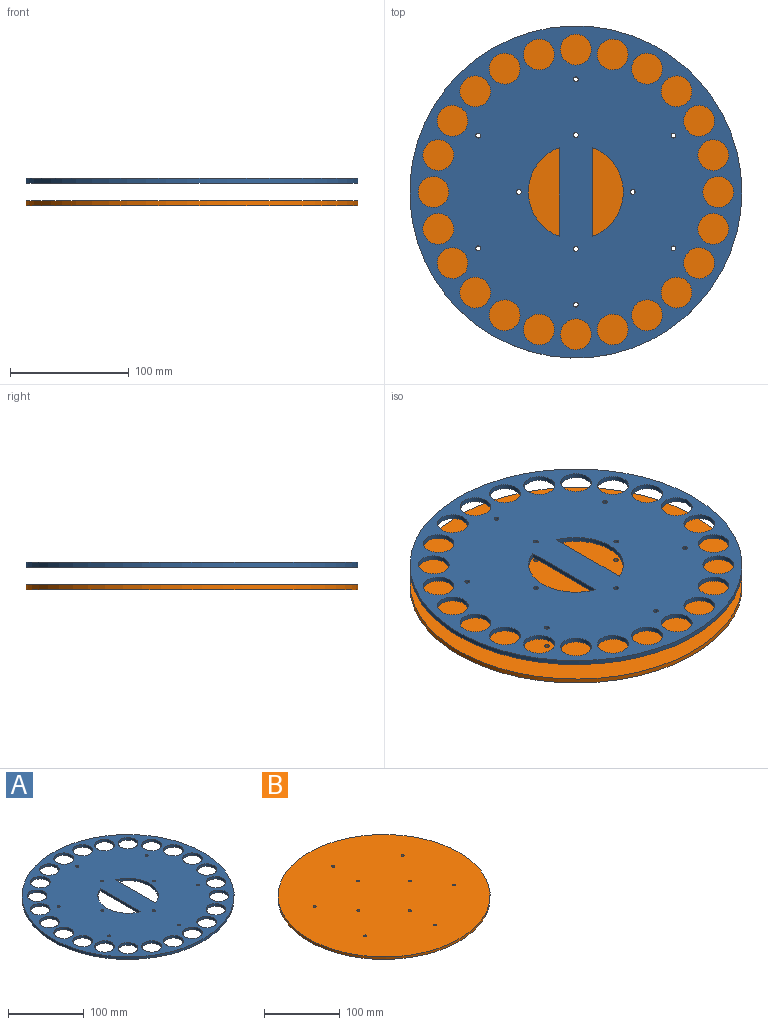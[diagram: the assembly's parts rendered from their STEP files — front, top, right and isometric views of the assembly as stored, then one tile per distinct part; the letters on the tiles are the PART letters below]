
ASSEMBLY  parts=2 mates=1
PART A: 41 faces, bbox 280x280x4 mm
  f0: plane 74.94x4mm, normal (-1,0,0), area 299.8mm2, adj f32,f39,f40
  f1: cylinder r=40mm len=74.94mm, axis (0,0,-1), area 388.2mm2, adj f37,f39,f40
  f2: cylinder r=13mm len=26mm, axis (0,0,-1), area 326.7mm2, adj f39,f40
  f3: cylinder r=13mm len=26mm, axis (0,0,-1), area 326.7mm2, adj f39,f40
  f4: cylinder r=13mm len=26mm, axis (0,0,-1), area 326.7mm2, adj f39,f40
  f5: cylinder r=13mm len=26mm, axis (0,0,-1), area 326.7mm2, adj f39,f40
  f6: cylinder r=13mm len=26mm, axis (0,0,-1), area 326.7mm2, adj f39,f40
  f7: cylinder r=13mm len=26mm, axis (0,0,-1), area 326.7mm2, adj f39,f40
  f8: cylinder r=13mm len=26mm, axis (0,0,-1), area 326.7mm2, adj f39,f40
  f9: cylinder r=13mm len=26mm, axis (0,0,-1), area 326.7mm2, adj f39,f40
  f10: cylinder r=13mm len=26mm, axis (0,0,-1), area 326.7mm2, adj f39,f40
  f11: cylinder r=13mm len=26mm, axis (0,0,-1), area 326.7mm2, adj f39,f40
  f12: cylinder r=13mm len=26mm, axis (0,0,-1), area 326.7mm2, adj f39,f40
  f13: cylinder r=13mm len=26mm, axis (0,0,-1), area 326.7mm2, adj f39,f40
  f14: cylinder r=13mm len=26mm, axis (0,0,-1), area 326.7mm2, adj f39,f40
  f15: cylinder r=13mm len=26mm, axis (0,0,-1), area 326.7mm2, adj f39,f40
  f16: cylinder r=13mm len=26mm, axis (0,0,-1), area 326.7mm2, adj f39,f40
  f17: cylinder r=13mm len=26mm, axis (0,0,-1), area 326.7mm2, adj f39,f40
  f18: cylinder r=13mm len=26mm, axis (0,0,-1), area 326.7mm2, adj f39,f40
  f19: cylinder r=13mm len=26mm, axis (0,0,-1), area 326.7mm2, adj f39,f40
  f20: cylinder r=13mm len=26mm, axis (0,0,-1), area 326.7mm2, adj f39,f40
  f21: cylinder r=13mm len=26mm, axis (0,0,-1), area 326.7mm2, adj f39,f40
  f22: cylinder r=13mm len=26mm, axis (0,0,-1), area 326.7mm2, adj f39,f40
  f23: cylinder r=13mm len=26mm, axis (0,0,-1), area 326.7mm2, adj f39,f40
  f24: cylinder r=13mm len=26mm, axis (0,0,-1), area 326.7mm2, adj f39,f40
  f25: cylinder r=13mm len=26mm, axis (0,0,-1), area 326.7mm2, adj f39,f40
  f26: cylinder r=2mm len=4mm, axis (0,0,-1), area 50.3mm2, adj f39,f40
  f27: cylinder r=2mm len=4mm, axis (0,0,-1), area 50.3mm2, adj f39,f40
  f28: cylinder r=2mm len=4mm, axis (0,0,-1), area 50.3mm2, adj f39,f40
  f29: cylinder r=2mm len=4mm, axis (0,0,-1), area 50.3mm2, adj f39,f40
  f30: cylinder r=2mm len=4mm, axis (0,0,-1), area 50.3mm2, adj f39,f40
  f31: cylinder r=2mm len=4mm, axis (0,0,-1), area 50.3mm2, adj f39,f40
  f32: cylinder r=40mm len=74.94mm, axis (0,0,-1), area 388.2mm2, adj f0,f39,f40
  f33: cylinder r=2mm len=4mm, axis (0,0,-1), area 50.3mm2, adj f39,f40
  f34: cylinder r=2mm len=4mm, axis (0,0,-1), area 50.3mm2, adj f39,f40
  f35: cylinder r=2mm len=4mm, axis (0,0,-1), area 50.3mm2, adj f39,f40
  f36: cylinder r=2mm len=4mm, axis (0,0,-1), area 50.3mm2, adj f39,f40
  f37: plane 74.94x4mm, normal (1,0,0), area 299.8mm2, adj f1,f39,f40
  f38: cylinder r=140mm len=280mm, axis (0,0,-1), area 3518.6mm2, adj f39,f40
  f39: plane 280x280mm, normal (0,0,1), area 45874.1mm2, adj f0,f1,f2,f3,f4,f5,f6,f7
  f40: plane 280x280mm, normal (0,0,-1), area 45874.1mm2, adj f0,f1,f2,f3,f4,f5,f6,f7
PART B: 13 faces, bbox 280x280x4 mm
  f0: cylinder r=2mm len=4mm, axis (0,0,-1), area 50.3mm2, adj f11,f12
  f1: cylinder r=2mm len=4mm, axis (0,0,-1), area 50.3mm2, adj f11,f12
  f2: cylinder r=2mm len=4mm, axis (0,0,-1), area 50.3mm2, adj f11,f12
  f3: cylinder r=2mm len=4mm, axis (0,0,-1), area 50.3mm2, adj f11,f12
  f4: cylinder r=2mm len=4mm, axis (0,0,-1), area 50.3mm2, adj f11,f12
  f5: cylinder r=2mm len=4mm, axis (0,0,-1), area 50.3mm2, adj f11,f12
  f6: cylinder r=2mm len=4mm, axis (0,0,-1), area 50.3mm2, adj f11,f12
  f7: cylinder r=2mm len=4mm, axis (0,0,-1), area 50.3mm2, adj f11,f12
  f8: cylinder r=2mm len=4mm, axis (0,0,-1), area 50.3mm2, adj f11,f12
  f9: cylinder r=140mm len=280mm, axis (0,0,-1), area 3518.6mm2, adj f11,f12
  f10: cylinder r=2mm len=4mm, axis (0,0,-1), area 50.3mm2, adj f11,f12
  f11: plane 280x280mm, normal (0,0,1), area 61449.6mm2, adj f0,f1,f2,f3,f4,f5,f6,f7
  f12: plane 280x280mm, normal (0,0,-1), area 61449.6mm2, adj f0,f1,f2,f3,f4,f5,f6,f7
PLACE A t=(-35.16,65,-3.96)mm
PLACE B t=(-335.16,65,-22.96)mm
MATE fastened B.f9 <-> A.f38  axis (0,0,-1) through (-35.16,65,-22.96)mm
